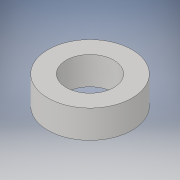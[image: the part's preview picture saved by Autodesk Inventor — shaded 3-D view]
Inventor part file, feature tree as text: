
AUTODESK INVENTOR PART (.ipt)
format: ipt  version: 2018 (Build 220112000, 112)  size: 95,744 bytes
history: native  units: in
note: dims shown in document units (in); Inventor stores cm internally (conversion verified against a paired STEP export)
features: extrude x1, sketch x1
ambient origin geometry x8: Origin, YZ Plane, XZ Plane, XY Plane, X Axis, Y Axis, Z Axis, Center Point
bodies: Solid1 (feature_tree)
feature tree (2):
  extrude  "Extrusion1"  Depth=0.1in
  sketch  "Sketch1"  dims[d0=0.17in d1=0.3in d2=0.1in d3=0.0in]
